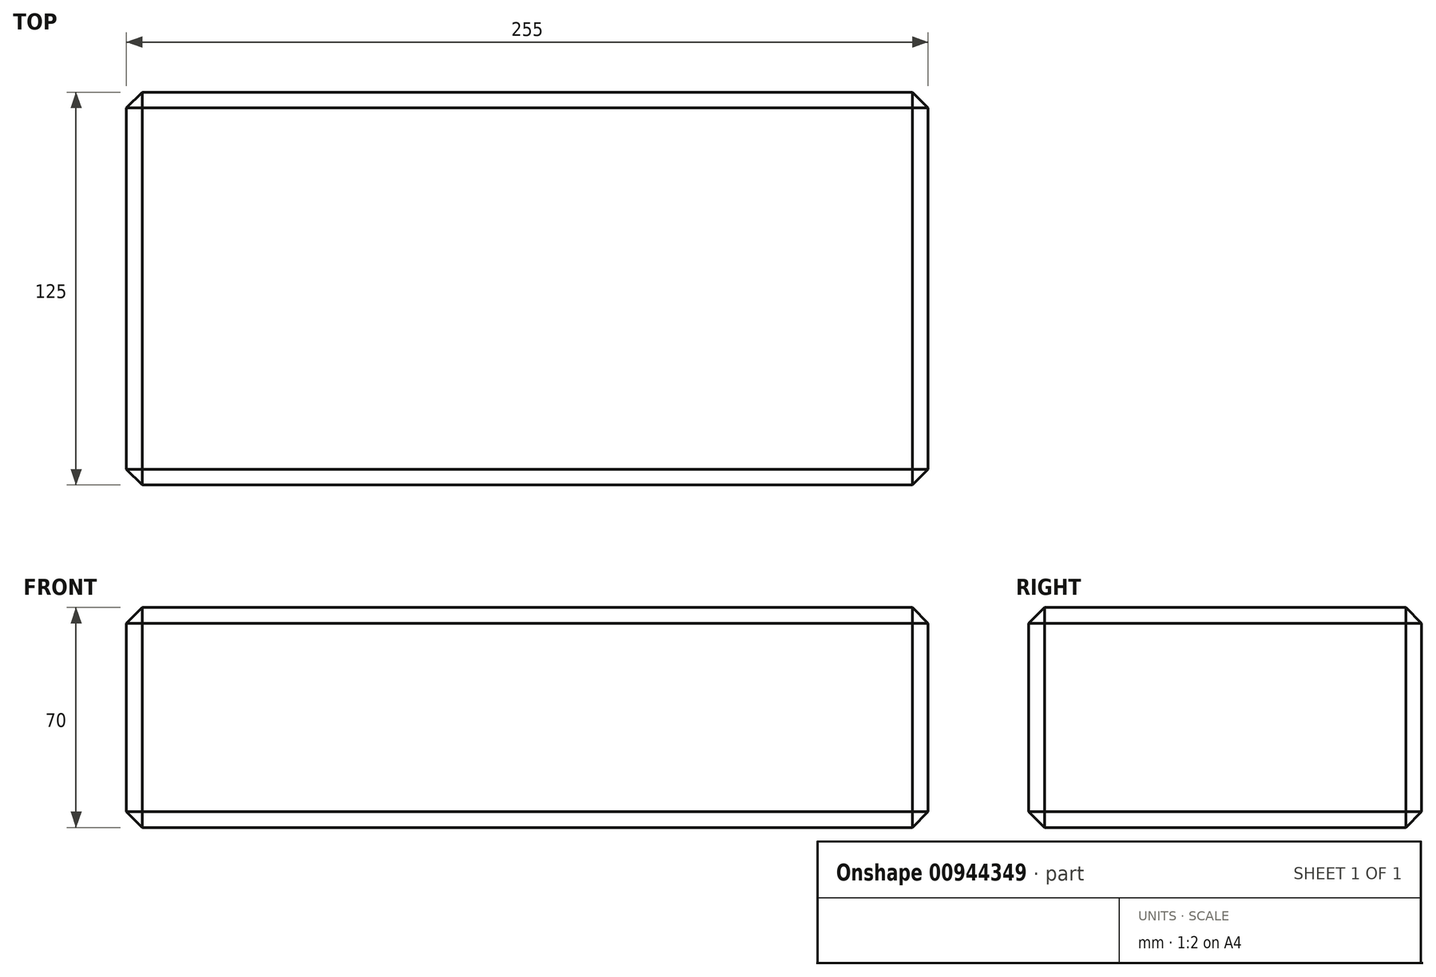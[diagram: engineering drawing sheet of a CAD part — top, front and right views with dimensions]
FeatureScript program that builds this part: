
annotation { "Feature Type Name" : "Feature", "Feature Type Description" : "" }
export const myFeature = defineFeature(function(context is Context, id is Id, definition is map)
    precondition{}
    {
        {
            var Q0;
            Q0=qCreatedBy(makeId("Top.planeOp"),FACE);
            var sketch = newSketch(context, id + "F0", { "sketchPlane" : qUnion([Q0])});
            skLineSegment(sketch, "E0", {"start": v(0, 0) * mm, "end": v(0, 125) * mm});
            skLineSegment(sketch, "E1", {"start": v(0, 125) * mm, "end": v(255, 125) * mm});
            skLineSegment(sketch, "E2", {"start": v(255, 125) * mm, "end": v(255, 0) * mm});
            skLineSegment(sketch, "E3", {"start": v(255, 0) * mm, "end": v(0, 0) * mm});
            skSolve(sketch);
        }
        {
            var Q0;
            Q0=qCreatedBy(makeId("Front.planeOp"),FACE);
            var sketch = newSketch(context, id + "F1", { "sketchPlane" : qUnion([Q0])});
            skLineSegment(sketch, "E4", {"start": v(0, 0) * mm, "end": v(0, 70) * mm});
            skSolve(sketch);
        }
        {
            var Q0;
            Q0=makeQuery(id+"F0.imprint","IMPRINT",FACE,{"disambiguationData":[TD([[makeQuery(id+"F0.imprint","IMPRINT",EDGE,{"derivedFrom":sQuery(id+"F0.wireOp",EDGE,"E0")}),-1.0]])]});
            var Q1;
            Q1=sQuery(id+"F1.wireOp",EDGE,"E4");
            sweep(context, id + "F2", {"profiles" : qUnion([Q0]), "path" : qUnion([Q1])});
        }
        {
            var Q0;
            Q0=makeQuery(id+"F2.opSweep","CAP_EDGE",EDGE,{"disambiguationData":[OSD([sQuery(id+"F0.wireOp",EDGE,"E3"),sQuery(id+"F1.wireOp",VERTEX,"E4.end")])],"isStart":false});
            var Q1;
            Q1=makeQuery(id+"F2.opSweep","CAP_EDGE",EDGE,{"disambiguationData":[OSD([sQuery(id+"F0.wireOp",EDGE,"E2"),sQuery(id+"F1.wireOp",VERTEX,"E4.end")])],"isStart":false});
            var Q2;
            Q2=makeQuery(id+"F2.opSweep","CAP_EDGE",EDGE,{"disambiguationData":[OSD([sQuery(id+"F0.wireOp",EDGE,"E0"),sQuery(id+"F1.wireOp",VERTEX,"E4.end")])],"isStart":false});
            var Q3;
            Q3=makeQuery(id+"F2.opSweep","CAP_EDGE",EDGE,{"disambiguationData":[OSD([sQuery(id+"F0.wireOp",EDGE,"E1"),sQuery(id+"F1.wireOp",VERTEX,"E4.end")])],"isStart":false});
            var Q4;
            Q4=makeQuery(id+"F2.opSweep","SWEPT_EDGE",EDGE,{"disambiguationData":[OSD([sQuery(id+"F0.wireOp",EDGE,"E2"),sQuery(id+"F0.wireOp",EDGE,"E3"),sQuery(id+"F1.wireOp",EDGE,"E4")])]});
            var Q5;
            Q5=makeQuery(id+"F2.opSweep","SWEPT_EDGE",EDGE,{"disambiguationData":[OSD([sQuery(id+"F0.wireOp",EDGE,"E1"),sQuery(id+"F0.wireOp",EDGE,"E2"),sQuery(id+"F1.wireOp",EDGE,"E4")])]});
            var Q6;
            Q6=makeQuery(id+"F2.opSweep","SWEPT_EDGE",EDGE,{"disambiguationData":[OSD([sQuery(id+"F0.wireOp",EDGE,"E0"),sQuery(id+"F0.wireOp",EDGE,"E3"),sQuery(id+"F1.wireOp",EDGE,"E4")])]});
            var Q7;
            Q7=makeQuery(id+"F2.opSweep","CAP_FACE",FACE,{"disambiguationData":[OSD([sQuery(id+"F0.wireOp",EDGE,"E0"),sQuery(id+"F0.wireOp",EDGE,"E1"),sQuery(id+"F0.wireOp",EDGE,"E2"),sQuery(id+"F0.wireOp",EDGE,"E3"),sQuery(id+"F1.wireOp",VERTEX,"E4.start")])],"isStart":true});
            var Q8;
            Q8=makeQuery(id+"F2.opSweep","SWEPT_EDGE",EDGE,{"disambiguationData":[OSD([sQuery(id+"F0.wireOp",EDGE,"E0"),sQuery(id+"F0.wireOp",EDGE,"E1"),sQuery(id+"F1.wireOp",EDGE,"E4")])]});
            chamfer(context, id + "F3", {"entities" : qUnion([Q0, Q1, Q2, Q3, Q4, Q5, Q6, Q7, Q8]), "width" : 5 * mm, "tangentPropagation" : true});
        }
    });
